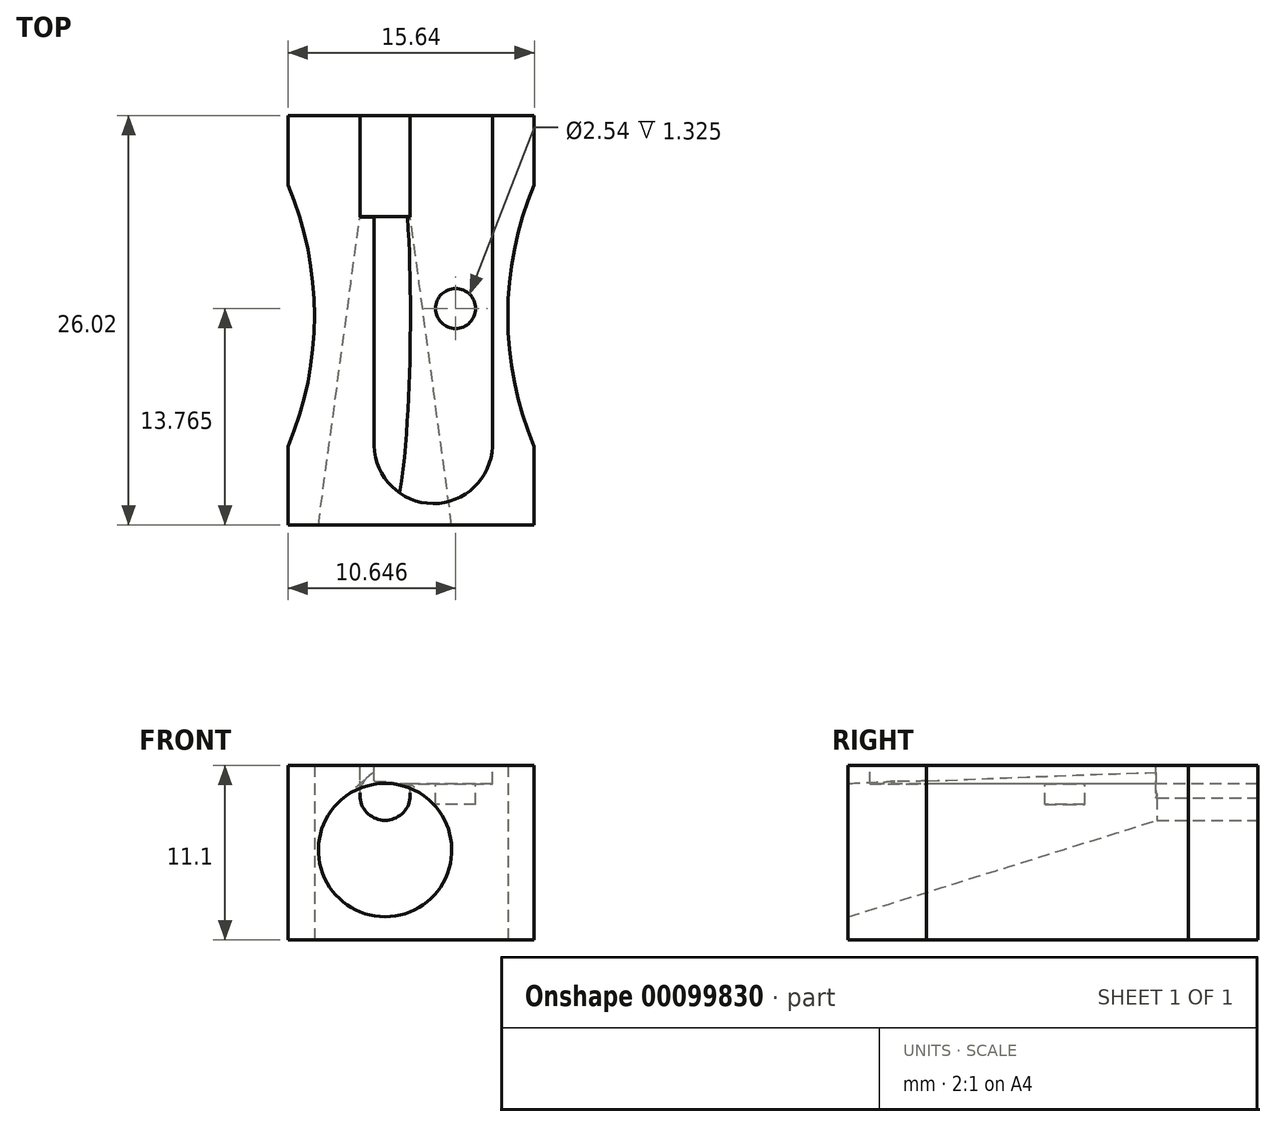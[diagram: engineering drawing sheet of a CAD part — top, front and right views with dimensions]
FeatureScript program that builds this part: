
annotation { "Feature Type Name" : "Feature", "Feature Type Description" : "" }
export const myFeature = defineFeature(function(context is Context, id is Id, definition is map)
    precondition{}
    {
        {
            var Q0;
            Q0=qCreatedBy(makeId("Top.planeOp"),FACE);
            var sketch = newSketch(context, id + "F0", { "sketchPlane" : qUnion([Q0])});
            skLineSegment(sketch, "E0.bottom", {"start": v(-7.82, 13) * mm, "end": v(0, 13) * mm});
            skLineSegment(sketch, "E0.top", {"start": v(-7.82, -13) * mm, "end": v(0, -13) * mm});
            skLineSegment(sketch, "E0.left", {"start": v(-7.82, 13) * mm, "end": v(-7.82, 8.6) * mm});
            skArc(sketch, "E1", {"start": v(-7.82, -8.02) * mm, "mid": v(-6.14, 0.29) * mm, "end": v(-7.82, 8.6) * mm});
            skPoint(sketch, "E2.orphan", {"position": v(7.81, -13) * mm});
            skLineSegment(sketch, "E3.MirrorCS", {"start": v(7.82, 13) * mm, "end": v(0, 13) * mm});
            skLineSegment(sketch, "E4.MirrorCS", {"start": v(7.82, 13) * mm, "end": v(7.81, 8.6) * mm});
            skLineSegment(sketch, "E5", {"start": v(-7.82, -8.02) * mm, "end": v(-7.82, -13) * mm});
            skLineSegment(sketch, "E6.MirrorCS", {"start": v(7.81, -8.02) * mm, "end": v(7.81, -13) * mm});
            skLineSegment(sketch, "E7.MirrorCS", {"start": v(7.82, -13) * mm, "end": v(0, -13) * mm});
            skArc(sketch, "E8.MirrorCS", {"start": v(7.82, -8.02) * mm, "mid": v(6.14, 0.29) * mm, "end": v(7.81, 8.6) * mm});
            skSolve(sketch);
        }
        {
            var Q0;
            Q0 = qSketchRegion(id + "F0", true);
            extrude(context, id + "F1", {"entities" : qUnion([Q0]), "depth" : 11.1 * mm});
        }
        {
            var Q0;
            Q0=makeQuery(id+"F1.opExtrude","SWEPT_FACE",FACE,{"disambiguationData":[OSD([sQuery(id+"F0.wireOp",EDGE,"E0.top"),sQuery(id+"F0.wireOp",EDGE,"E7.MirrorCS")])]});
            var sketch = newSketch(context, id + "F2", { "sketchPlane" : qUnion([Q0])});
            skCircle(sketch, "E9", {"center": v(-1.66, 5.71) * mm, "radius": 4.24 * mm});
            skSolve(sketch);
        }
        {
            var Q0;
            Q0=makeQuery(id+"F1.opExtrude","CAP_FACE",FACE,{"disambiguationData":[OSD([sQuery(id+"F0.wireOp",EDGE,"E0.bottom"),sQuery(id+"F0.wireOp",EDGE,"E0.top"),sQuery(id+"F0.wireOp",EDGE,"E0.left"),sQuery(id+"F0.wireOp",EDGE,"E1"),sQuery(id+"F0.wireOp",EDGE,"E3.MirrorCS"),sQuery(id+"F0.wireOp",EDGE,"E4.MirrorCS"),sQuery(id+"F0.wireOp",EDGE,"E5"),sQuery(id+"F0.wireOp",EDGE,"E6.MirrorCS"),sQuery(id+"F0.wireOp",EDGE,"E7.MirrorCS"),sQuery(id+"F0.wireOp",EDGE,"E8.MirrorCS")])],"isStart":false});
            var sketch = newSketch(context, id + "F3", { "sketchPlane" : qUnion([Q0])});
            skLineSegment(sketch, "E10", {"start": v(5.17, 13) * mm, "end": v(5.17, -8.02) * mm});
            skLineSegment(sketch, "E11", {"start": v(-2.35, -7.96) * mm, "end": v(-2.35, 13) * mm});
            skArc(sketch, "E12", {"start": v(-2.35, -7.96) * mm, "mid": v(1.52, -11.63) * mm, "end": v(5.17, -7.74) * mm});
            skLineSegment(sketch, "E13", {"start": v(-2.35, 13) * mm, "end": v(5.17, 13) * mm});
            skSolve(sketch);
        }
        {
            var Q0;
            {var subQ3=sQuery(id+"F3.wireOp",EDGE,"E11");Q0=makeQuery(id+"F3.imprint","IMPRINT",FACE,{"disambiguationData":[TD([[makeQuery(id+"F3.imprint","IMPRINT",EDGE,{"derivedFrom":subQ3}),-1.0]])]});}
            var sketch = newSketch(context, id + "F4", { "sketchPlane" : qUnion([Q0])});
            skCircle(sketch, "E14", {"center": v(2.83, 0.76) * mm, "radius": 1.27 * mm});
            skSolve(sketch);
        }
        {
            var Q0;
            Q0=makeQuery(id+"F1.opExtrude","SWEPT_FACE",FACE,{"disambiguationData":[OSD([sQuery(id+"F0.wireOp",EDGE,"E0.bottom"),sQuery(id+"F0.wireOp",EDGE,"E3.MirrorCS")])]});
            var sketch = newSketch(context, id + "F5", { "sketchPlane" : qUnion([Q0])});
            skCircle(sketch, "E15", {"center": v(1.66, 9.2) * mm, "radius": 1.6 * mm});
            skSolve(sketch);
        }
        {
            var Q0;
            Q0 = qSketchRegion(id + "F5", true);
            extrude(context, id + "F6", {"entities" : qUnion([Q0]), "operationType" : NewBodyOperationType.REMOVE, "oppositeDirection" : true, "depth" : 6.4 * mm});
        }
        {
            var Q0;
            Q0=makeQuery(id+"F2.imprint","IMPRINT",FACE,{"disambiguationData":[TD([[makeQuery(id+"F2.imprint","IMPRINT",EDGE,{"derivedFrom":sQuery(id+"F2.wireOp",EDGE,"E9")}),1.0]])]});
            var Q1;
            Q1=makeQuery(id+"F6.boolean.opBoolean","COPY",FACE,{"derivedFrom":makeQuery(id+"F6.opExtrude","CAP_FACE",FACE,{"disambiguationData":[OSD([sQuery(id+"F5.wireOp",EDGE,"E15")])],"isStart":false})});
            loft(context, id + "F7", {"operationType" : NewBodyOperationType.REMOVE, "sheetProfilesArray" : [{ "sheetProfileEntities" : qUnion([Q0]) }, { "sheetProfileEntities" : qUnion([Q1]) }]});
        }
        {
            var Q0;
            {var subQ3=sQuery(id+"F3.wireOp",EDGE,"E11");Q0=makeQuery(id+"F3.imprint","IMPRINT",FACE,{"disambiguationData":[TD([[makeQuery(id+"F3.imprint","IMPRINT",EDGE,{"derivedFrom":subQ3}),-1.0]])]});}
            extrude(context, id + "F8", {"entities" : qUnion([Q0]), "operationType" : NewBodyOperationType.REMOVE, "oppositeDirection" : true, "depth" : 1.18 * mm});
        }
        {
            var Q0;
            {var subQ9=sQuery(id+"F3.wireOp",EDGE,"E11");Q0=makeQuery(id+"F3.imprint","IMPRINT",FACE,{"disambiguationData":[TD([[makeQuery(id+"F3.imprint","IMPRINT",EDGE,{"derivedFrom":subQ9}),1.0]])]});}
            var sketch = newSketch(context, id + "F9", { "sketchPlane" : qUnion([Q0])});
            skLineSegment(sketch, "E16", {"start": v(-3.26, 13.05) * mm, "end": v(-0.06, 13.05) * mm});
            skLineSegment(sketch, "E17", {"start": v(-0.06, 13.05) * mm, "end": v(-0.06, 6.55) * mm});
            skLineSegment(sketch, "E18", {"start": v(-0.06, 6.55) * mm, "end": v(-3.26, 6.55) * mm});
            skLineSegment(sketch, "E19", {"start": v(-3.26, 6.55) * mm, "end": v(-3.26, 13.05) * mm});
            skSolve(sketch);
        }
        {
            var Q0;
            Q0 = qSketchRegion(id + "F9", true);
            extrude(context, id + "F10", {"entities" : qUnion([Q0]), "operationType" : NewBodyOperationType.REMOVE, "oppositeDirection" : true, "depth" : 2.07 * mm});
        }
        {
            var Q0;
            Q0 = qSketchRegion(id + "F4", true);
            extrude(context, id + "F11", {"entities" : qUnion([Q0]), "operationType" : NewBodyOperationType.REMOVE, "oppositeDirection" : true, "depth" : 2.5 * mm});
        }
    });
